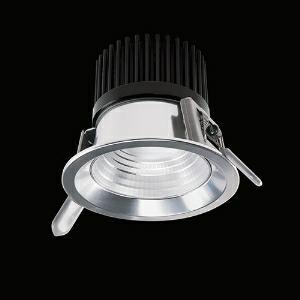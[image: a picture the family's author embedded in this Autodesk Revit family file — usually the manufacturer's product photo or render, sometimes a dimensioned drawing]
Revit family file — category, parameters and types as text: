
# Revit family: spectral_myral_myral_3500-840-m
name_source: partatom
category: Lighting Fixtures
revit_build: Autodesk Revit 2016 (Build: 20150220_1215(x64)
units: mm (PartAtom-declared; Revit-internal decimal feet)

## family parameters
Cut with Voids When Loaded = No
Host = Face
Light Source = No
Part Type = Normal
Room Calculation Point = No
Round Connector Dimension = Use Diameter
Shared = No

## types (1)
- SPECTRAL MYRAL (1 x )
    Apparent Load = 0 VA
    Approval mark = CE
    CIE Flux Codes = 82 99 100 100 100
    Control Gear = Electronic transformer
    Default Elevation = 1800 mm
    Description = SPG0320181
MYRAL recessed spot

Design:
    Height = 0 mm  [stored 0 ft]
    Lamp = 1 x
    Lamp count = 1
    Length = 120 mm
    Luminous efficacy = 0 lm/W
    Manufacturer = Ridi
    ModVariant = No
    Model = MYRAL 3500-840-M
    Mounting Place = Ceiling
    Mounting Type = Recessed
    Number of Poles = 1
    OnlyDefault = Yes
    Power Factor = 1
    Product Name = SPECTRAL MYRAL
    Product group = Downlight recessed
    ProductGroupID = 400
    Protection Class = Protection class
    Protection Degree = IP 20
    RlxData = <blob elided: 38669 chars, md5=b750d6aa>
    Socket = socket
    Standby Power = 0 W
    System Light Flux = 0 lm
    System Power = 0 W
    Type Image = myral_04.jpg
    URL = http://reluxnet.relux.com
    VarID = ---
    Voltage = 0 V
    Weight = 0.00 kg
    Width = 0 mm  [stored 0 ft]

note: [stored X ft] marks values corroborated as IEEE doubles in the binary element streams (Revit-internal decimal feet)

## geometry (parser evidence)
native form markers: Sweep x11
no freeform markers — native parametric forms only
